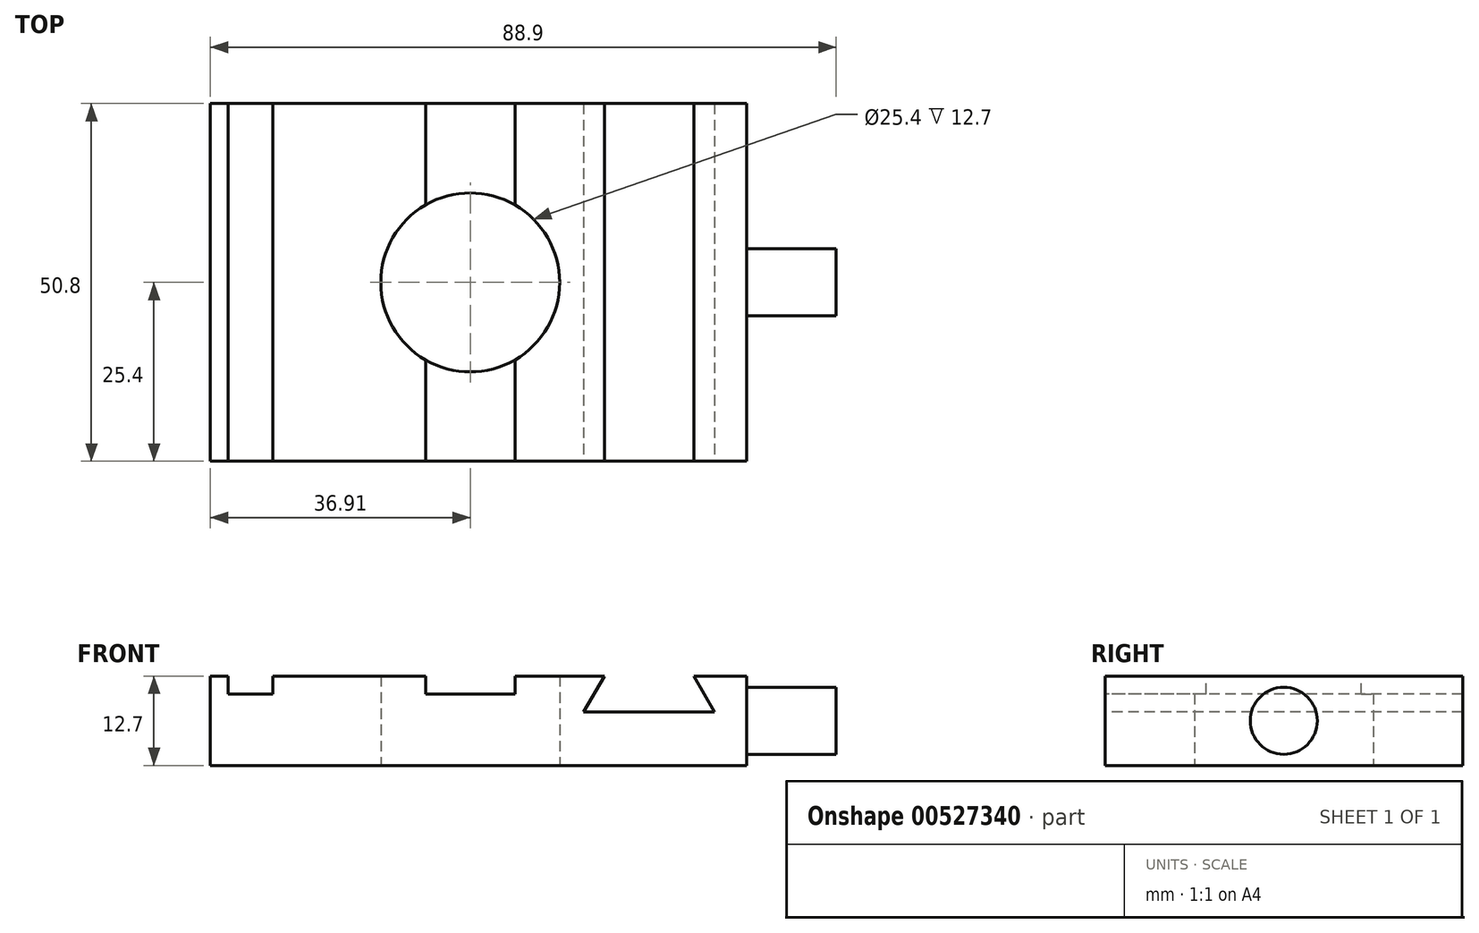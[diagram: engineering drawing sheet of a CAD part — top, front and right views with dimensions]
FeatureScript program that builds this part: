
annotation { "Feature Type Name" : "Feature", "Feature Type Description" : "" }
export const myFeature = defineFeature(function(context is Context, id is Id, definition is map)
    precondition{}
    {
        {
            var Q0;
            Q0=qCreatedBy(makeId("Top.planeOp"),FACE);
            var sketch = newSketch(context, id + "F0", { "sketchPlane" : qUnion([Q0])});
            skLineSegment(sketch, "E0.bottom", {"start": v(-36.9, 25.4) * mm, "end": v(39.3, 25.4) * mm});
            skLineSegment(sketch, "E0.top", {"start": v(-36.9, -25.4) * mm, "end": v(39.3, -25.4) * mm});
            skLineSegment(sketch, "E0.left", {"start": v(-36.9, 25.4) * mm, "end": v(-36.9, -25.4) * mm});
            skLineSegment(sketch, "E0.right", {"start": v(39.3, 25.4) * mm, "end": v(39.3, -25.4) * mm});
            skPoint(sketch, "E0.middle", {"position": v(1.2, 0) * mm});
            skCircle(sketch, "E1", {"center": v(0, 0) * mm, "radius": 12.7 * mm});
            skSolve(sketch);
        }
        {
            var Q0;
            Q0 = qSketchRegion(id + "F0", true);
            extrude(context, id + "F1", {"entities" : qUnion([Q0]), "depth" : 12.7 * mm, "offsetDistance" : 25.4 * mm});
        }
        {
            var Q0;
            Q0=makeQuery(id+"F1.opExtrude","CAP_FACE",FACE,{"disambiguationData":[OSD([sQuery(id+"F0.wireOp",EDGE,"E0.bottom"),sQuery(id+"F0.wireOp",EDGE,"E0.top"),sQuery(id+"F0.wireOp",EDGE,"E0.left"),sQuery(id+"F0.wireOp",EDGE,"E0.right"),sQuery(id+"F0.wireOp",EDGE,"E1")])],"isStart":false});
            var sketch = newSketch(context, id + "F2", { "sketchPlane" : qUnion([Q0])});
            skLineSegment(sketch, "E2.bottom", {"start": v(-34.37, 25.4) * mm, "end": v(-28.02, 25.4) * mm});
            skLineSegment(sketch, "E2.top", {"start": v(-34.37, -25.4) * mm, "end": v(-28.02, -25.4) * mm});
            skLineSegment(sketch, "E2.left", {"start": v(-34.37, 25.4) * mm, "end": v(-34.37, -25.4) * mm});
            skLineSegment(sketch, "E2.right", {"start": v(-28.02, 25.4) * mm, "end": v(-28.02, -25.4) * mm});
            skLineSegment(sketch, "E3.bottom", {"start": v(-6.35, 25.4) * mm, "end": v(6.35, 25.4) * mm});
            skLineSegment(sketch, "E3.top", {"start": v(-6.35, -25.4) * mm, "end": v(6.35, -25.4) * mm});
            skLineSegment(sketch, "E3.left", {"start": v(-6.35, 25.4) * mm, "end": v(-6.35, -25.4) * mm});
            skLineSegment(sketch, "E3.right", {"start": v(6.35, 25.4) * mm, "end": v(6.35, -25.4) * mm});
            skPoint(sketch, "E3.middle", {"position": v(0, 0) * mm});
            skSolve(sketch);
        }
        {
            var Q0;
            Q0=makeQuery(id+"F2.imprint","IMPRINT",FACE,{"disambiguationData":[TD([[makeQuery(id+"F2.imprint","IMPRINT",EDGE,{"derivedFrom":sQuery(id+"F2.wireOp",EDGE,"E2.bottom")}),-1.0]])]});
            var Q1;
            {var subQ0=sQuery(id+"F2.wireOp",EDGE,"E3.top");Q1=makeQuery(id+"F2.imprint","IMPRINT",FACE,{"disambiguationData":[TD([[makeQuery(id+"F2.imprint","IMPRINT",EDGE,{"derivedFrom":subQ0}),1.0]])]});}
            var Q2;
            {var subQ0=sQuery(id+"F2.wireOp",EDGE,"E3.bottom");Q2=makeQuery(id+"F2.imprint","IMPRINT",FACE,{"disambiguationData":[TD([[makeQuery(id+"F2.imprint","IMPRINT",EDGE,{"derivedFrom":subQ0}),-1.0]])]});}
            extrude(context, id + "F3", {"entities" : qUnion([Q0, Q1, Q2]), "operationType" : NewBodyOperationType.REMOVE, "oppositeDirection" : true, "depth" : 2.54 * mm, "offsetDistance" : 25.4 * mm});
        }
        {
            var Q0;
            Q0=makeQuery(id+"F1.opExtrude","SWEPT_FACE",FACE,{"disambiguationData":[OSD([sQuery(id+"F0.wireOp",EDGE,"E0.top")])]});
            var sketch = newSketch(context, id + "F4", { "sketchPlane" : qUnion([Q0])});
            skLineSegment(sketch, "E4", {"start": v(19.05, 12.7) * mm, "end": v(31.75, 12.7) * mm});
            skLineSegment(sketch, "E5", {"start": v(19.05, 12.7) * mm, "end": v(16.12, 7.62) * mm});
            skLineSegment(sketch, "E6", {"start": v(16.12, 7.62) * mm, "end": v(34.68, 7.62) * mm});
            skLineSegment(sketch, "E7", {"start": v(34.68, 7.62) * mm, "end": v(31.75, 12.7) * mm});
            skLineSegment(sketch, "E8", {"start": v(25.4, 7.62) * mm, "end": v(25.4, 12.7) * mm, "construction": true});
            skSolve(sketch);
        }
        {
            var Q0;
            Q0=makeQuery(id+"F4.imprint","IMPRINT",FACE,{"disambiguationData":[TD([[makeQuery(id+"F4.imprint","IMPRINT",EDGE,{"derivedFrom":sQuery(id+"F4.wireOp",EDGE,"E4")}),-1.0]])]});
            extrude(context, id + "F5", {"entities" : qUnion([Q0]), "operationType" : NewBodyOperationType.REMOVE, "oppositeDirection" : true, "depth" : 50.8 * mm, "offsetDistance" : 25.4 * mm});
        }
        {
            var Q0;
            Q0=makeQuery(id+"F1.opExtrude","SWEPT_FACE",FACE,{"disambiguationData":[OSD([sQuery(id+"F0.wireOp",EDGE,"E0.right")])]});
            var sketch = newSketch(context, id + "F6", { "sketchPlane" : qUnion([Q0])});
            skCircle(sketch, "E9", {"center": v(0, 6.35) * mm, "radius": 4.76 * mm});
            skPoint(sketch, "E9.centerSnap0", {"position": v(-25.4, 6.35) * mm});
            skPoint(sketch, "E9.centerSnap1", {"position": v(0, 12.7) * mm});
            skSolve(sketch);
        }
        {
            var Q0;
            Q0=makeQuery(id+"F6.imprint","IMPRINT",FACE,{"disambiguationData":[TD([[makeQuery(id+"F6.imprint","IMPRINT",EDGE,{"derivedFrom":sQuery(id+"F6.wireOp",EDGE,"E9")}),1.0]])]});
            extrude(context, id + "F7", {"entities" : qUnion([Q0]), "operationType" : NewBodyOperationType.ADD, "depth" : 12.7 * mm, "offsetDistance" : 25.4 * mm});
        }
    });
